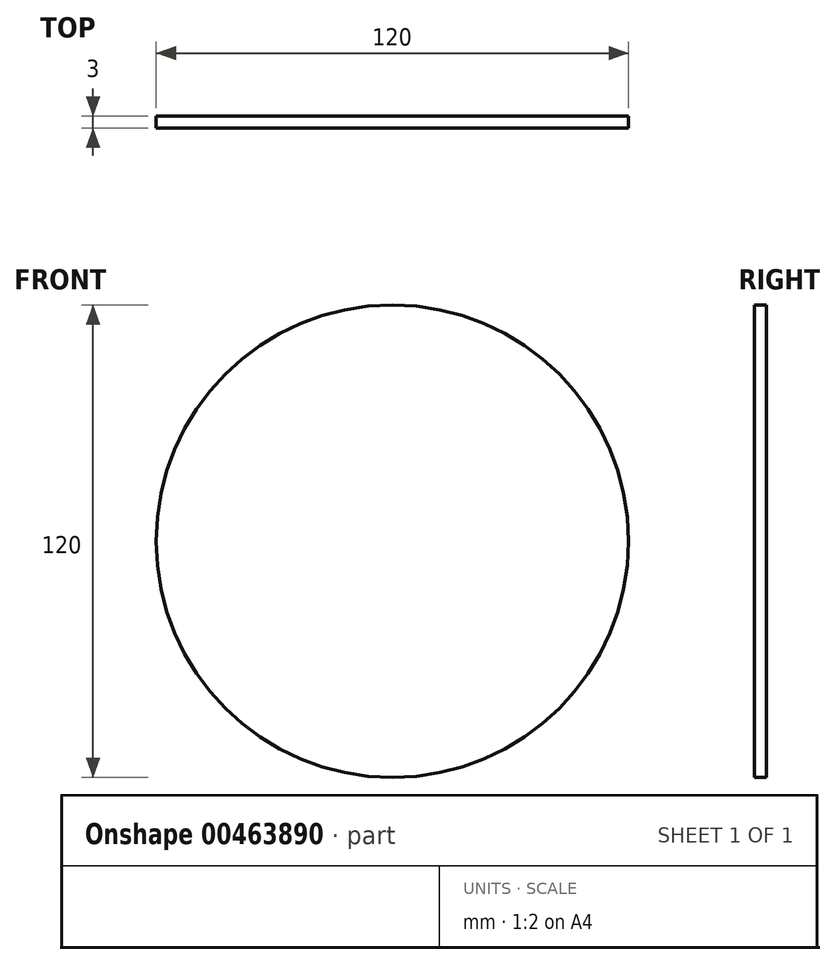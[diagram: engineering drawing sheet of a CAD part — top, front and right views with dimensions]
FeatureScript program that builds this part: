
annotation { "Feature Type Name" : "Feature", "Feature Type Description" : "" }
export const myFeature = defineFeature(function(context is Context, id is Id, definition is map)
    precondition{}
    {
        {
            var Q0;
            Q0=qCreatedBy(makeId("Front.planeOp"),FACE);
            var sketch = newSketch(context, id + "F0", { "sketchPlane" : qUnion([Q0])});
            skCircle(sketch, "E0", {"center": v(0, 0) * mm, "radius": 60 * mm});
            skSolve(sketch);
        }
        {
            var Q0;
            Q0 = qSketchRegion(id + "F0", true);
            extrude(context, id + "F1", {"entities" : qUnion([Q0]), "depth" : 3 * mm});
        }
    });
